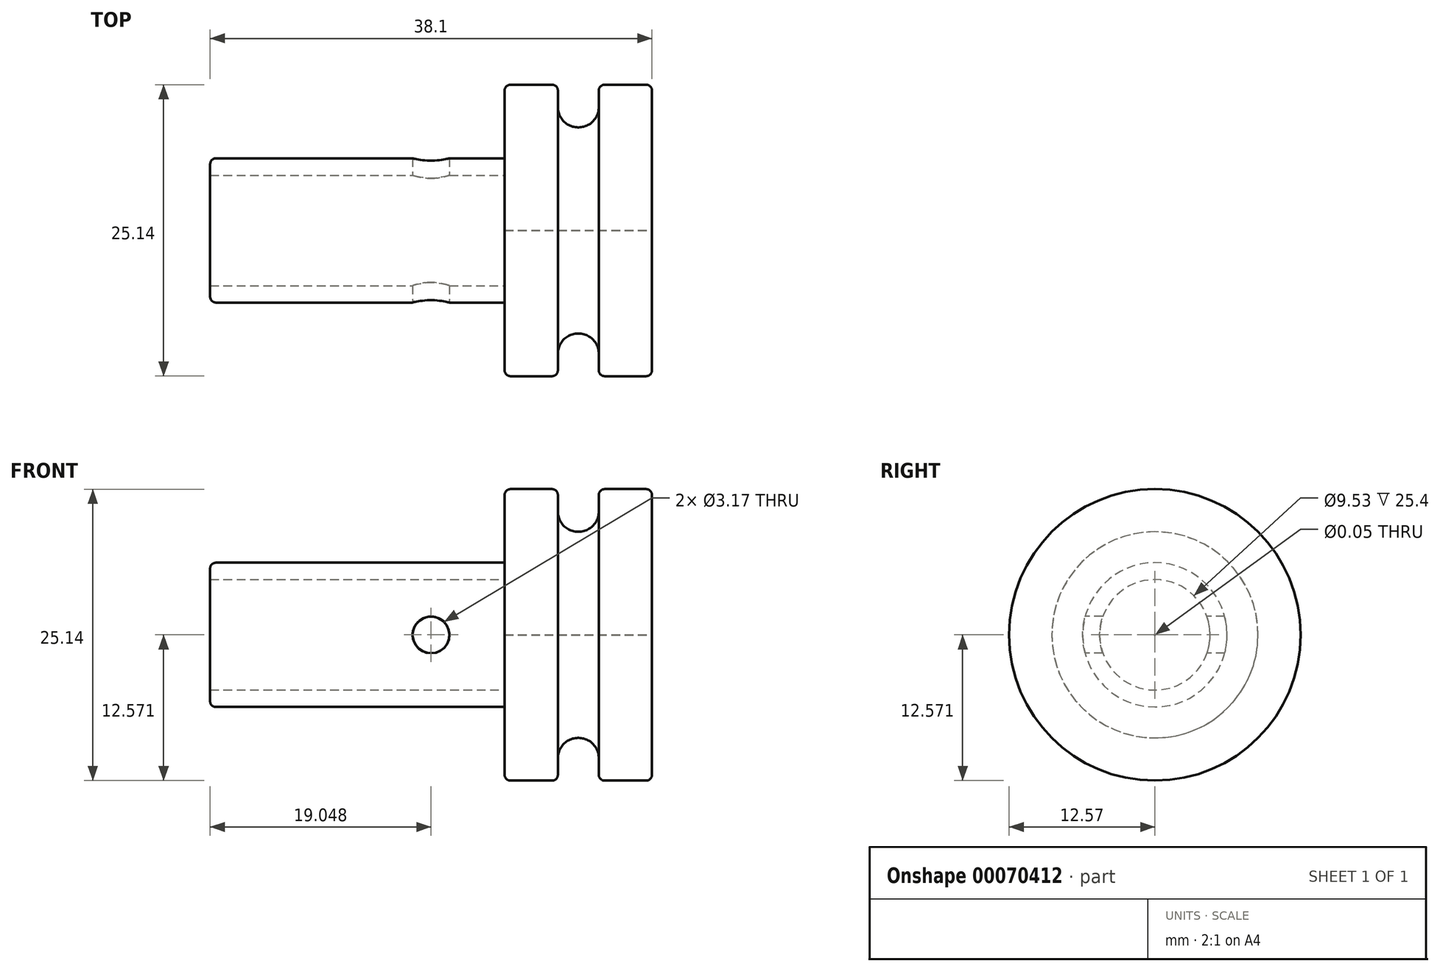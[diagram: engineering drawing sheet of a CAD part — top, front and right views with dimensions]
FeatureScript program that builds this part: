
annotation { "Feature Type Name" : "Feature", "Feature Type Description" : "" }
export const myFeature = defineFeature(function(context is Context, id is Id, definition is map)
    precondition{}
    {
        {
            var Q0;
            Q0=qCreatedBy(makeId("Front.planeOp"),FACE);
            var sketch = newSketch(context, id + "F0", { "sketchPlane" : qUnion([Q0])});
            skLineSegment(sketch, "E0", {"start": v(-49.51, -32.69) * mm, "end": v(-36.81, -32.69) * mm});
            skLineSegment(sketch, "E1", {"start": v(-36.81, -32.69) * mm, "end": v(-36.81, -20.12) * mm});
            skLineSegment(sketch, "E2", {"start": v(-36.81, -20.12) * mm, "end": v(-41.4, -20.12) * mm});
            skLineSegment(sketch, "E3", {"start": v(-41.4, -20.12) * mm, "end": v(-41.4, -23.8) * mm});
            skLineSegment(sketch, "E4", {"start": v(-41.4, -23.8) * mm, "end": v(-44.93, -23.8) * mm});
            skLineSegment(sketch, "E5", {"start": v(-44.93, -23.8) * mm, "end": v(-44.93, -20.12) * mm});
            skLineSegment(sketch, "E6", {"start": v(-44.93, -20.12) * mm, "end": v(-49.51, -20.12) * mm});
            skLineSegment(sketch, "E7", {"start": v(-49.51, -20.12) * mm, "end": v(-49.51, -32.69) * mm});
            skSolve(sketch);
        }
        {
            var Q0;
            Q0=makeQuery(id+"F0.imprint","IMPRINT",FACE,{"disambiguationData":[TD([[makeQuery(id+"F0.imprint","IMPRINT",EDGE,{"derivedFrom":sQuery(id+"F0.wireOp",EDGE,"E0")}),1.0]])]});
            var Q1;
            Q1=sQuery(id+"F0.wireOp",EDGE,"E0");
            revolve(context, id + "F1", {"entities" : qUnion([Q0]), "axis" : qUnion([Q1]), "revolveType" : RevolveType.FULL});
        }
        {
            var Q0;
            Q0=makeQuery(id+"F1.opRevolve","SWEPT_FACE",FACE,{"disambiguationData":[OSD([sQuery(id+"F0.wireOp",EDGE,"E7")])]});
            var sketch = newSketch(context, id + "F2", { "sketchPlane" : qUnion([Q0])});
            skCircle(sketch, "E8", {"center": v(0, -32.69) * mm, "radius": 6.22 * mm});
            skCircle(sketch, "E9", {"center": v(0, -32.69) * mm, "radius": 4.76 * mm});
            skSolve(sketch);
        }
        {
            var Q0;
            Q0 = qSketchRegion(id + "F2", true);
            extrude(context, id + "F3", {"entities" : qUnion([Q0]), "operationType" : NewBodyOperationType.ADD, "depth" : 25.4 * mm});
        }
        {
            var Q0;
            Q0=qCreatedBy(makeId("Front.planeOp"),FACE);
            var sketch = newSketch(context, id + "F4", { "sketchPlane" : qUnion([Q0])});
            skCircle(sketch, "E10", {"center": v(-55.86, -32.69) * mm, "radius": 1.59 * mm});
            skSolve(sketch);
        }
        {
            var Q0;
            Q0 = qSketchRegion(id + "F4", true);
            extrude(context, id + "F5", {"entities" : qUnion([Q0]), "operationType" : NewBodyOperationType.REMOVE, "endBound" : BoundingType.SYMMETRIC, "oppositeDirection" : true, "depth" : 25.4 * mm});
        }
        {
            var Q0;
            Q0=makeQuery(id+"F1.opRevolve","SWEPT_EDGE",EDGE,{"disambiguationData":[OSD([sQuery(id+"F0.wireOp",EDGE,"E3"),sQuery(id+"F0.wireOp",EDGE,"E4")])]});
            var Q1;
            Q1=makeQuery(id+"F1.opRevolve","SWEPT_EDGE",EDGE,{"disambiguationData":[OSD([sQuery(id+"F0.wireOp",EDGE,"E4"),sQuery(id+"F0.wireOp",EDGE,"E5")])]});
            fillet(context, id + "F6", {"entities" : qUnion([Q0, Q1]), "radius" : 1.74 * mm, "tangentPropagation" : true, "allowEdgeOverflow" : false});
        }
        {
            var Q0;
            Q0=makeQuery(id+"F1.opRevolve","SWEPT_EDGE",EDGE,{"disambiguationData":[OSD([sQuery(id+"F0.wireOp",EDGE,"E6"),sQuery(id+"F0.wireOp",EDGE,"E7")])]});
            var Q1;
            Q1=makeQuery(id+"F3.opExtrude","CAP_EDGE",EDGE,{"disambiguationData":[OSD([sQuery(id+"F2.wireOp",EDGE,"E8")])],"isStart":true});
            var Q2;
            Q2=makeQuery(id+"F3.opExtrude","CAP_EDGE",EDGE,{"disambiguationData":[OSD([sQuery(id+"F2.wireOp",EDGE,"E8")])],"isStart":false});
            var Q3;
            Q3=makeQuery(id+"F1.opRevolve","SWEPT_EDGE",EDGE,{"disambiguationData":[OSD([sQuery(id+"F0.wireOp",EDGE,"E1"),sQuery(id+"F0.wireOp",EDGE,"E2")])]});
            var Q4;
            Q4=makeQuery(id+"F1.opRevolve","SWEPT_EDGE",EDGE,{"disambiguationData":[OSD([sQuery(id+"F0.wireOp",EDGE,"E2"),sQuery(id+"F0.wireOp",EDGE,"E3")])]});
            var Q5;
            Q5=makeQuery(id+"F1.opRevolve","SWEPT_EDGE",EDGE,{"disambiguationData":[OSD([sQuery(id+"F0.wireOp",EDGE,"E5"),sQuery(id+"F0.wireOp",EDGE,"E6")])]});
            fillet(context, id + "F7", {"entities" : qUnion([Q0, Q1, Q2, Q3, Q4, Q5]), "radius" : 0.5 * mm, "tangentPropagation" : true, "allowEdgeOverflow" : false});
        }
        {
            var Q0;
            Q0=makeQuery(id+"F1.opRevolve","SWEPT_FACE",FACE,{"disambiguationData":[OSD([sQuery(id+"F0.wireOp",EDGE,"E1")])]});
            var sketch = newSketch(context, id + "F8", { "sketchPlane" : qUnion([Q0])});
            skCircle(sketch, "E11", {"center": v(0, -32.69) * mm, "radius": 0.03 * mm});
            skSolve(sketch);
        }
        {
            var Q0;
            Q0 = qSketchRegion(id + "F8", true);
            extrude(context, id + "F9", {"entities" : qUnion([Q0]), "operationType" : NewBodyOperationType.REMOVE, "endBound" : BoundingType.THROUGH_ALL, "oppositeDirection" : true, "depth" : 25.4 * mm});
        }
    });
